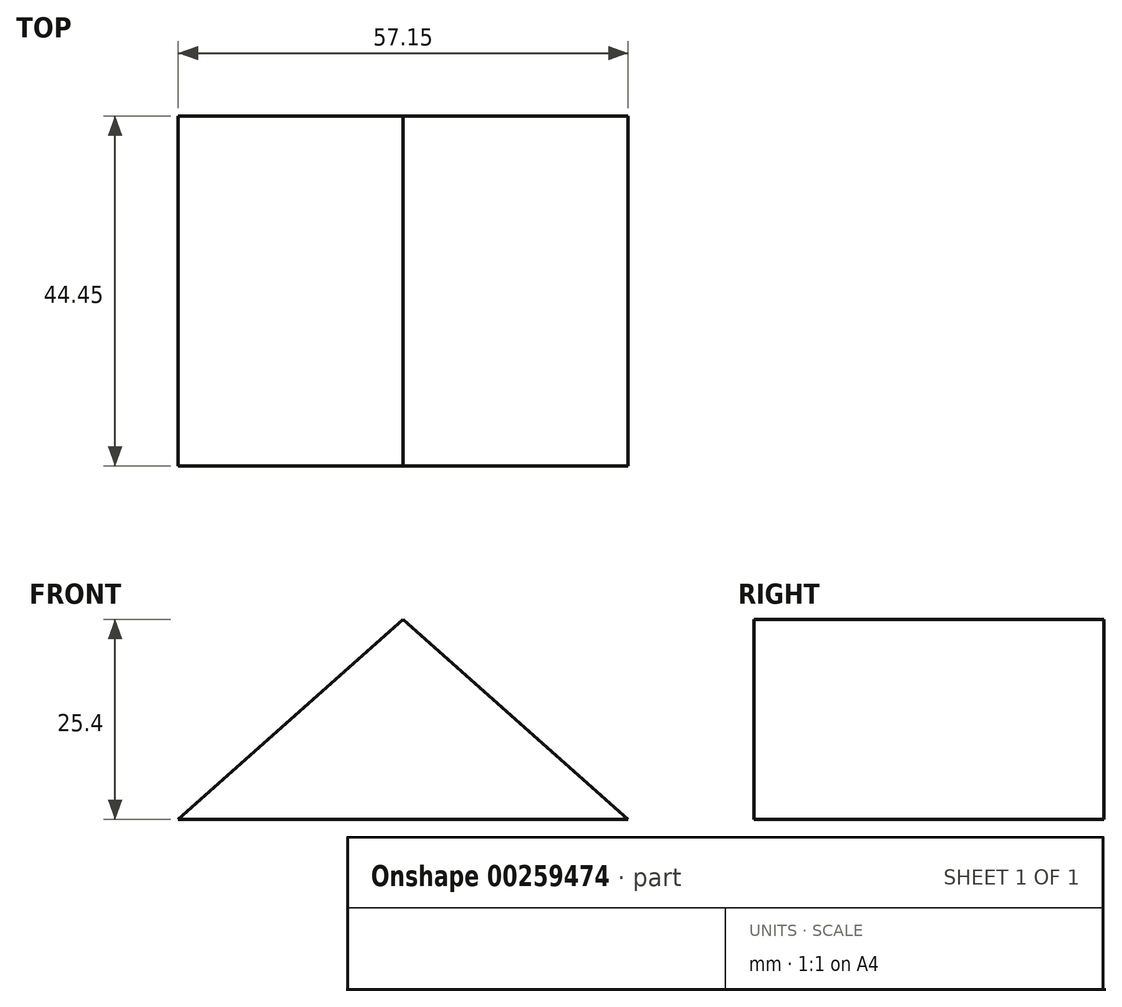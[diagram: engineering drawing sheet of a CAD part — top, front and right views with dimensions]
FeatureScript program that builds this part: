
annotation { "Feature Type Name" : "Feature", "Feature Type Description" : "" }
export const myFeature = defineFeature(function(context is Context, id is Id, definition is map)
    precondition{}
    {
        {
            var Q0;
            Q0=qCreatedBy(makeId("Front.planeOp"),FACE);
            var sketch = newSketch(context, id + "F0", { "sketchPlane" : qUnion([Q0])});
            skLineSegment(sketch, "E0", {"start": v(0, 0) * mm, "end": v(57.15, 0) * mm});
            skLineSegment(sketch, "E1", {"start": v(57.15, 0) * mm, "end": v(28.57, 25.4) * mm});
            skLineSegment(sketch, "E2", {"start": v(28.57, 25.4) * mm, "end": v(0, 0) * mm});
            skPoint(sketch, "E3", {"position": v(28.58, 0) * mm});
            skPoint(sketch, "E4", {"position": v(28.57, 25.4) * mm});
            skSolve(sketch);
        }
        {
            var Q0;
            Q0=makeQuery(id+"F0.imprint","IMPRINT",FACE,{"disambiguationData":[TD([[makeQuery(id+"F0.imprint","IMPRINT",EDGE,{"derivedFrom":sQuery(id+"F0.wireOp",EDGE,"E0")}),1.0]])]});
            extrude(context, id + "F1", {"entities" : qUnion([Q0]), "depth" : 44.45 * mm});
        }
    });
